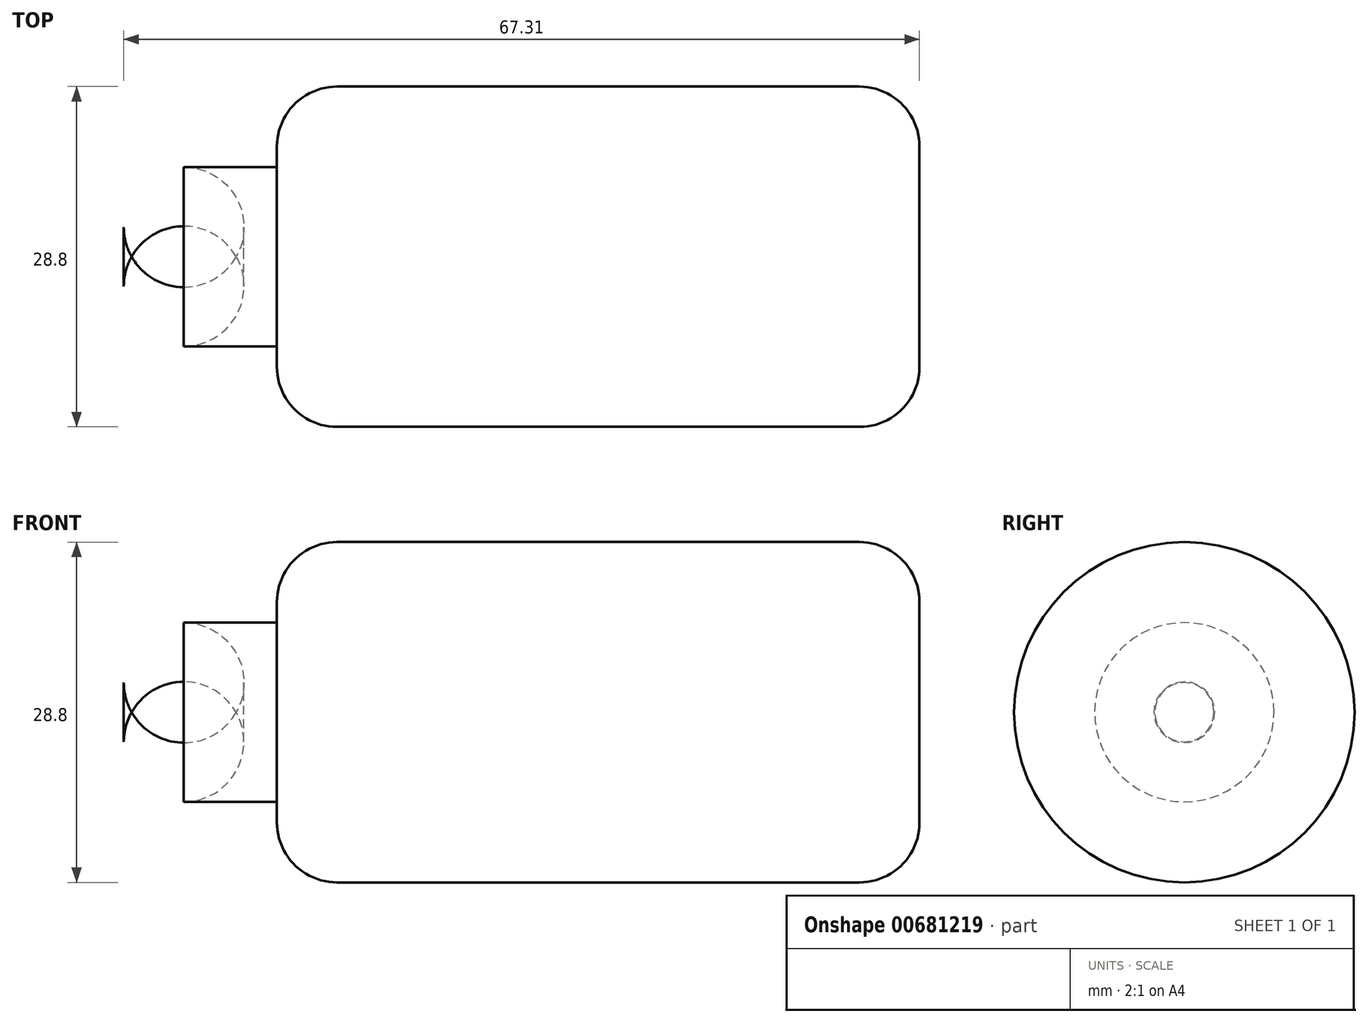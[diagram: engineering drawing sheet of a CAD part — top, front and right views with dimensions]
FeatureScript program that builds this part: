
annotation { "Feature Type Name" : "Feature", "Feature Type Description" : "" }
export const myFeature = defineFeature(function(context is Context, id is Id, definition is map)
    precondition{}
    {
        {
            var Q0;
            Q0=qCreatedBy(makeId("Front.planeOp"),FACE);
            var sketch = newSketch(context, id + "F0", { "sketchPlane" : qUnion([Q0])});
            skLineSegment(sketch, "E0", {"start": v(0, 0) * mm, "end": v(0, 7.58) * mm});
            skLineSegment(sketch, "E1", {"start": v(0, 7.58) * mm, "end": v(12.95, 7.58) * mm});
            skLineSegment(sketch, "E2", {"start": v(12.95, 7.58) * mm, "end": v(12.95, 14.4) * mm});
            skLineSegment(sketch, "E3", {"start": v(12.95, 14.4) * mm, "end": v(67.31, 14.4) * mm});
            skLineSegment(sketch, "E4", {"start": v(67.31, 14.4) * mm, "end": v(67.31, 0) * mm});
            skLineSegment(sketch, "E5", {"start": v(67.31, 0) * mm, "end": v(0, 0) * mm});
            skSolve(sketch);
        }
        {
            var Q0;
            Q0=makeQuery(id+"F0.imprint","IMPRINT",FACE,{"disambiguationData":[TD([[makeQuery(id+"F0.imprint","IMPRINT",EDGE,{"derivedFrom":sQuery(id+"F0.wireOp",EDGE,"E0")}),-1.0]])]});
            var Q1;
            Q1=sQuery(id+"F0.wireOp",EDGE,"E5");
            revolve(context, id + "F1", {"entities" : qUnion([Q0]), "axis" : qUnion([Q1]), "revolveType" : RevolveType.FULL});
        }
        {
            var Q0;
            Q0=makeQuery(id+"F1.opRevolve","SWEPT_FACE",FACE,{"disambiguationData":[OSD([sQuery(id+"F0.wireOp",EDGE,"E3")])]});
            var Q1;
            Q1=makeQuery(id+"F1.opRevolve","SWEPT_EDGE",EDGE,{"disambiguationData":[OSD([sQuery(id+"F0.wireOp",EDGE,"E0"),sQuery(id+"F0.wireOp",EDGE,"E1")])]});
            fillet(context, id + "F2", {"entities" : qUnion([Q0, Q1]), "radius" : 5.08 * mm, "tangentPropagation" : true, "allowEdgeOverflow" : false});
        }
    });
